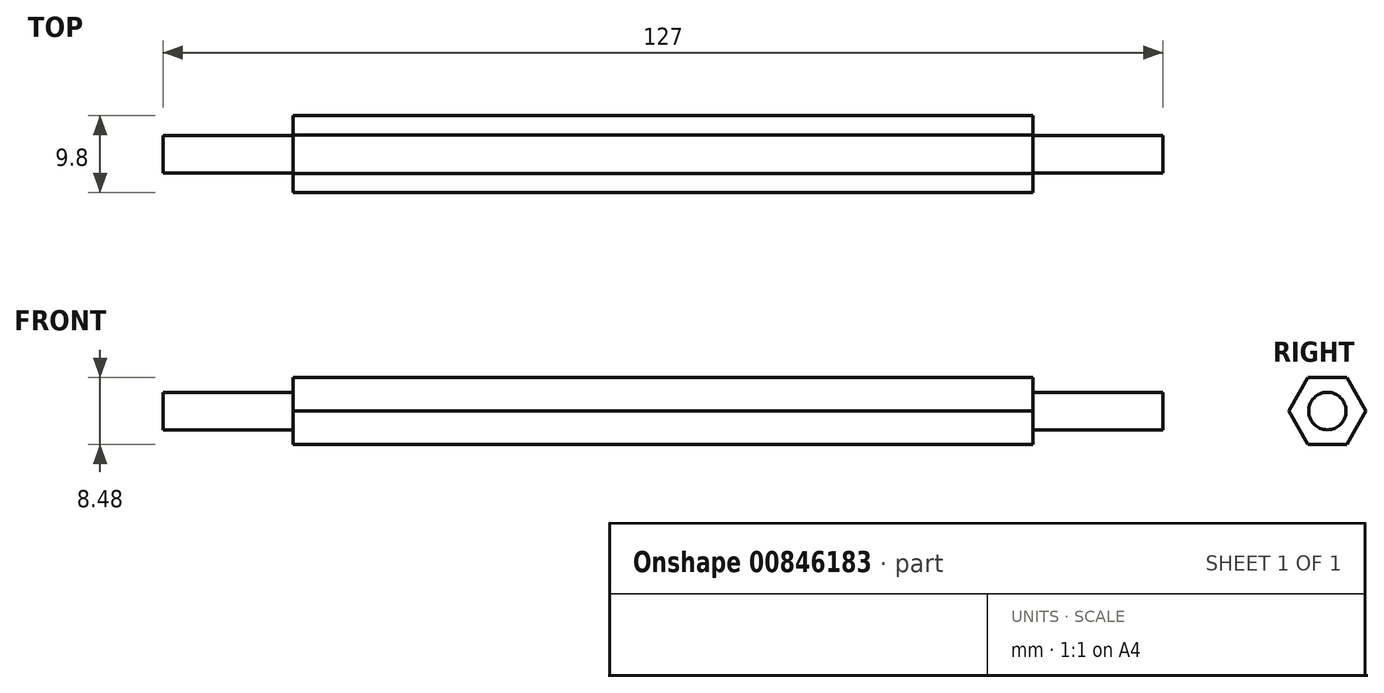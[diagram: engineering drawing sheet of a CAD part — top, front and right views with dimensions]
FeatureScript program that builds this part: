
annotation { "Feature Type Name" : "Feature", "Feature Type Description" : "" }
export const myFeature = defineFeature(function(context is Context, id is Id, definition is map)
    precondition{}
    {
        {
            var Q0;
            Q0=qCreatedBy(makeId("Right.planeOp"),FACE);
            var sketch = newSketch(context, id + "F0", { "sketchPlane" : qUnion([Q0])});
            skCircle(sketch, "E0.cCircle", {"center": v(0, 0) * mm, "radius": 4.9 * mm, "construction": true});
            skLineSegment(sketch, "E0.0", {"start": v(4.9, 0) * mm, "end": v(2.45, -4.24) * mm});
            skLineSegment(sketch, "E0.1", {"start": v(2.45, -4.24) * mm, "end": v(-2.45, -4.24) * mm});
            skLineSegment(sketch, "E0.2", {"start": v(-2.45, -4.24) * mm, "end": v(-4.9, 0) * mm});
            skLineSegment(sketch, "E0.3", {"start": v(-4.9, 0) * mm, "end": v(-2.45, 4.24) * mm});
            skLineSegment(sketch, "E0.4", {"start": v(-2.45, 4.24) * mm, "end": v(2.45, 4.24) * mm});
            skLineSegment(sketch, "E0.5", {"start": v(2.45, 4.24) * mm, "end": v(4.9, 0) * mm});
            skSolve(sketch);
        }
        {
            var Q0;
            Q0 = qSketchRegion(id + "F0", true);
            extrude(context, id + "F1", {"entities" : qUnion([Q0]), "endBound" : BoundingType.SYMMETRIC, "depth" : 93.98 * mm, "offsetDistance" : 25.4 * mm});
        }
        {
            var Q0;
            Q0=qCreatedBy(makeId("Right.planeOp"),FACE);
            var sketch = newSketch(context, id + "F2", { "sketchPlane" : qUnion([Q0])});
            skCircle(sketch, "E1", {"center": v(0, 0) * mm, "radius": 2.38 * mm});
            skSolve(sketch);
        }
        {
            var Q0;
            Q0 = qSketchRegion(id + "F2", true);
            extrude(context, id + "F3", {"entities" : qUnion([Q0]), "operationType" : NewBodyOperationType.ADD, "endBound" : BoundingType.SYMMETRIC, "depth" : 127 * mm, "offsetDistance" : 25.4 * mm});
        }
    });
